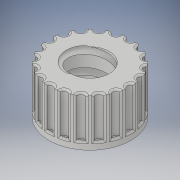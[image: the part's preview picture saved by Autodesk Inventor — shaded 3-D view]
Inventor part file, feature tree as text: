
AUTODESK INVENTOR PART (.ipt)
format: ipt  version: 2019 (Build 230136000, 136)  size: 489,984 bytes
history: native  units: mm
features: sketch x5, extrude x4, fillet x2, pattern_circular x1, other x1
ambient origin geometry x8: Origin, YZ Plane, XZ Plane, XY Plane, X Axis, Y Axis, Z Axis, Center Point
bodies: Volumenkörper1 (feature_tree)
feature tree (13):
  extrude  "Oberkörper"  Depth=5.0mm
  extrude  "Unterkörper"  Depth=18.4mm
  extrude  "Ausschnitt Griff"  Depth=5.0mm TaperAngle=0.0deg
  fillet  "Rundung1"  Radius=2.0mm
  pattern_circular  "Runde Anordnung1"  Count=20 Angle=360.0deg
  extrude  "Extrusion6"  Depth=0.5mm
  other  "Spirale3"
  fillet  "Rundung5"  Radius=10.7mm
  sketch  "Skizze2"  dims[d0=12.6mm d1=5.0mm]
  sketch  "Skizze3"  dims[d2=8.0mm d3=0.0mm d4=18.4mm]
  sketch  "Skizze4"  dims[d5=22.6mm d6=5.0mm d7=0.0mm d8=2.0mm]
  sketch  "Skizze8"  dims[d9=11.0mm d10=0.0mm]
  sketch  "Skizze9"  dims[d11=0.5mm d12=200.0mm d13=360.0deg d42=12.6mm d43=10.7mm d44=8.0mm d45=0.0mm d51=5.0mm d52=10.0mm d53=30.0mm d54=0.0mm d55=90.0deg d56=90.0deg d57=0.0mm d58=0.0mm d59=0.5mm]
